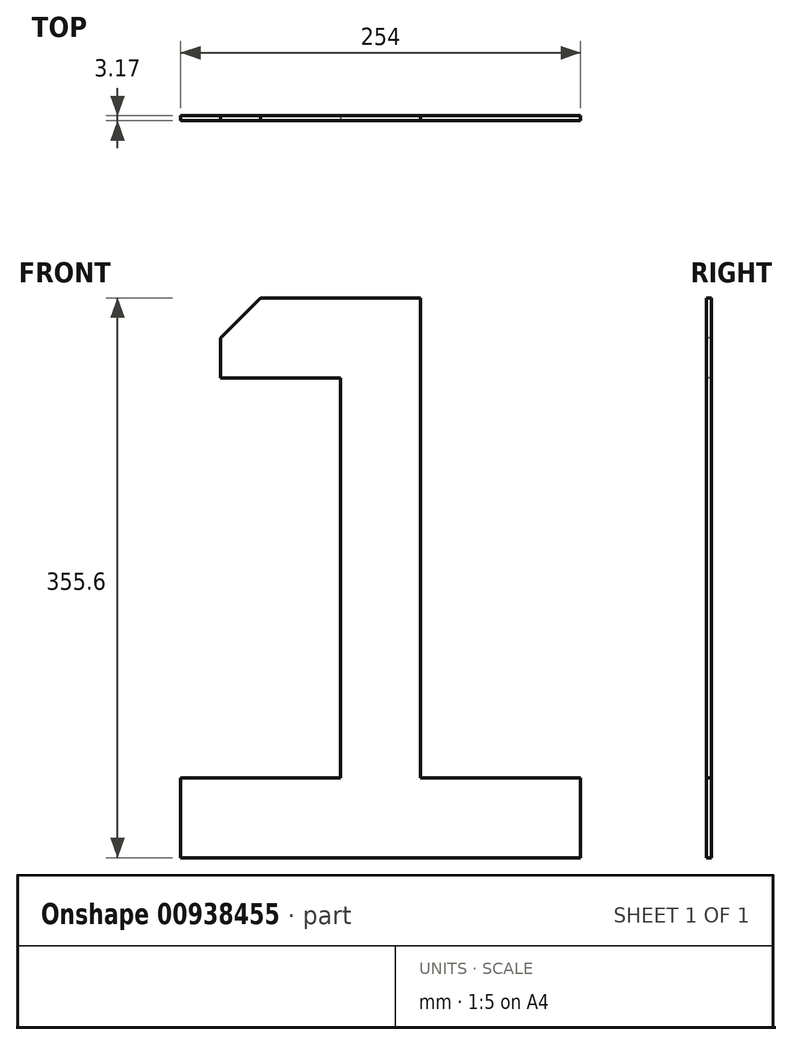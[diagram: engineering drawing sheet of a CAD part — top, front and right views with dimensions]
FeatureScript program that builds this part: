
annotation { "Feature Type Name" : "Feature", "Feature Type Description" : "" }
export const myFeature = defineFeature(function(context is Context, id is Id, definition is map)
    precondition{}
    {
        {
            var Q0;
            Q0=qCreatedBy(makeId("Front.planeOp"),FACE);
            var sketch = newSketch(context, id + "F0", { "sketchPlane" : qUnion([Q0])});
            skLineSegment(sketch, "E0.bottom", {"start": v(0, 0) * mm, "end": v(-254, 0) * mm});
            skLineSegment(sketch, "E0.top", {"start": v(0, 50.8) * mm, "end": v(-101.6, 50.8) * mm});
            skLineSegment(sketch, "E0.left", {"start": v(0, 0) * mm, "end": v(0, 50.8) * mm});
            skLineSegment(sketch, "E0.right", {"start": v(-254, 0) * mm, "end": v(-254, 50.8) * mm});
            skLineSegment(sketch, "E1.left", {"start": v(-101.6, 50.8) * mm, "end": v(-101.6, 304.8) * mm});
            skLineSegment(sketch, "E1.right", {"start": v(-152.4, 50.8) * mm, "end": v(-152.4, 304.8) * mm});
            skLineSegment(sketch, "E2.bottom", {"start": v(-152.4, 304.8) * mm, "end": v(-228.6, 304.8) * mm});
            skLineSegment(sketch, "E2.top", {"start": v(-101.6, 355.6) * mm, "end": v(-203.2, 355.6) * mm});
            skLineSegment(sketch, "E2.left", {"start": v(-101.6, 304.8) * mm, "end": v(-101.6, 355.6) * mm});
            skLineSegment(sketch, "E2.right", {"start": v(-228.6, 304.8) * mm, "end": v(-228.6, 330.2) * mm});
            skLineSegment(sketch, "E3", {"start": v(-228.6, 330.2) * mm, "end": v(-203.2, 355.6) * mm});
            skLineSegment(sketch, "E4.trimOffspring", {"start": v(-152.4, 50.8) * mm, "end": v(-254, 50.8) * mm});
            skSolve(sketch);
        }
        {
            var Q0;
            Q0=makeQuery(id+"F0.imprint","IMPRINT",FACE,{"disambiguationData":[TD([[makeQuery(id+"F0.imprint","IMPRINT",EDGE,{"derivedFrom":sQuery(id+"F0.wireOp",EDGE,"E0.bottom")}),-1.0]])]});
            extrude(context, id + "F1", {"entities" : qUnion([Q0]), "oppositeDirection" : true, "depth" : 3.17 * mm, "offsetDistance" : 25.4 * mm});
        }
    });
